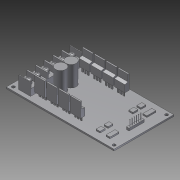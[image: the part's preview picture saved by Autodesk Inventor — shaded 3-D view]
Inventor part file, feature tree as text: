
AUTODESK INVENTOR PART (.ipt)
format: ipt  version: 2011 SP2 (Build 150309200, 309)  size: 477,696 bytes
history: native  units: mm
features: extrude x13, projected_geometry x8, sketch x7, fillet x1
ambient origin geometry x8: Origin, YZ Plane, XZ Plane, XY Plane, X Axis, Y Axis, Z Axis, Center Point
bodies: Solid1 (feature_tree)
feature tree (29):
  extrude  "Extrusion1"  Depth=54.075mm
  sketch  "Sketch2"  dims[d2=60.0mm d3=30.0mm]
  extrude  "Extrusion2"  Depth=30.0mm
  extrude  "Extrusion3"  Depth=3.0mm
  extrude  "Extrusion4"  Depth=3.0mm
  extrude  "Extrusion5"  Depth=2.15mm
  fillet  "Fillet1"  Radius=2.0mm
  extrude  "Extrusion6"  Depth=2.0mm
  extrude  "Extrusion7"  Depth=2.15mm
  extrude  "Extrusion8"  Depth=2.15mm
  extrude  "Extrusion9"  Depth=2.15mm
  extrude  "Extrusion10"  Depth=52.0mm
  extrude  "Extrusion11"  Depth=11.9mm
  extrude  "Extrusion12"  Depth=8.45mm
  extrude  "Extrusion13"  Depth=4.0mm
  sketch  "Sketch1"  dims[d0=108.15mm d1=54.075mm]
  sketch  "Sketch3"  dims[d4=1.6mm d5=0.0mm d6=3.0mm]
  projected_geometry  "Projected Loop1"
  projected_geometry  "Projected Loop2"
  projected_geometry  "Projected Loop3"
  projected_geometry  "Projected Loop4"
  projected_geometry  "Projected Loop5"
  sketch  "Sketch4"  dims[d7=3.0mm d8=3.0mm]
  projected_geometry  "Projected Loop6"
  sketch  "Sketch5"  dims[d9=3.0mm d10=2.15mm d11=2.0mm]
  projected_geometry  "Projected Loop7"
  sketch  "Sketch6"  dims[d12=2.0mm d13=2.0mm]
  projected_geometry  "Projected Loop8"
  sketch  "Sketch7"  dims[d15=2.0mm d16=2.15mm d17=2.15mm d18=2.15mm d19=52.0mm d20=11.9mm d21=8.45mm d22=4.0mm d23=0.6mm d24=0.6mm d25=2.6mm d27=43.45mm d28=8.275mm d29=4.0mm d30=5.0mm d31=21.4mm d32=15.3mm d33=2.5mm d34=25.0mm d35=15.0mm d36=7.0mm d37=7.0mm d38=46.0mm d39=4.0mm d40=9.0mm d41=7.0mm d42=7.0mm d43=3.0mm d44=3.0mm d45=8.2mm d46=1.6mm d47=0.0mm d48=1.3mm d49=1.3mm d50=1.3mm d51=0.65mm d52=1.3mm d53=1.3mm d54=0.65mm d55=7.36mm d56=7.36mm d57=7.36mm d58=7.36mm d59=7.36mm d60=12.5mm d61=0.0mm d62=6.6mm d63=0.0mm d64=5.0mm d65=5.0mm d66=5.0mm d67=5.0mm d68=5.0mm d69=5.0mm d70=4.0mm d71=0.0mm d72=2.0mm d73=4.35mm d74=0.0mm d75=4.45mm d76=1.0mm d77=1.0mm d78=4.45mm d79=14.55mm d80=0.0mm d81=6.65mm d82=105.0deg d83=1.3mm d84=105.0deg d85=1.3mm d86=14.55mm d87=0.0mm d88=10.3mm d89=1.6mm d90=1.6mm d91=1.6mm d92=10.3mm d93=10.3mm d99=1.5mm d101=1.5mm d106=1.55mm d107=1.55mm d108=1.55mm d109=1.325mm d110=1.5mm d111=1.5mm d112=1.55mm d113=1.55mm d114=1.325mm d115=1.55mm d116=1.55mm d117=1.55mm d118=1.55mm d119=1.55mm d120=1.55mm d121=1.55mm d122=1.5mm d123=1.5mm d124=1.325mm d125=1.5mm d126=1.5mm d127=1.325mm d128=53.3mm d129=0.0mm d130=2.5mm d131=0.0mm d132=2.185mm d133=2.186mm d134=2.185mm d135=2.186mm d136=2.186mm d137=2.186mm d138=0.6mm d139=0.6mm d140=0.6mm d141=0.6mm d142=0.6mm d143=0.6mm d144=5.9mm d145=0.0mm d146=1.5mm d147=0.0mm d148=4.3mm d149=4.3mm d150=10.3mm d151=10.3mm d152=10.45mm d153=24.775mm d154=20.4mm d155=0.0mm]
